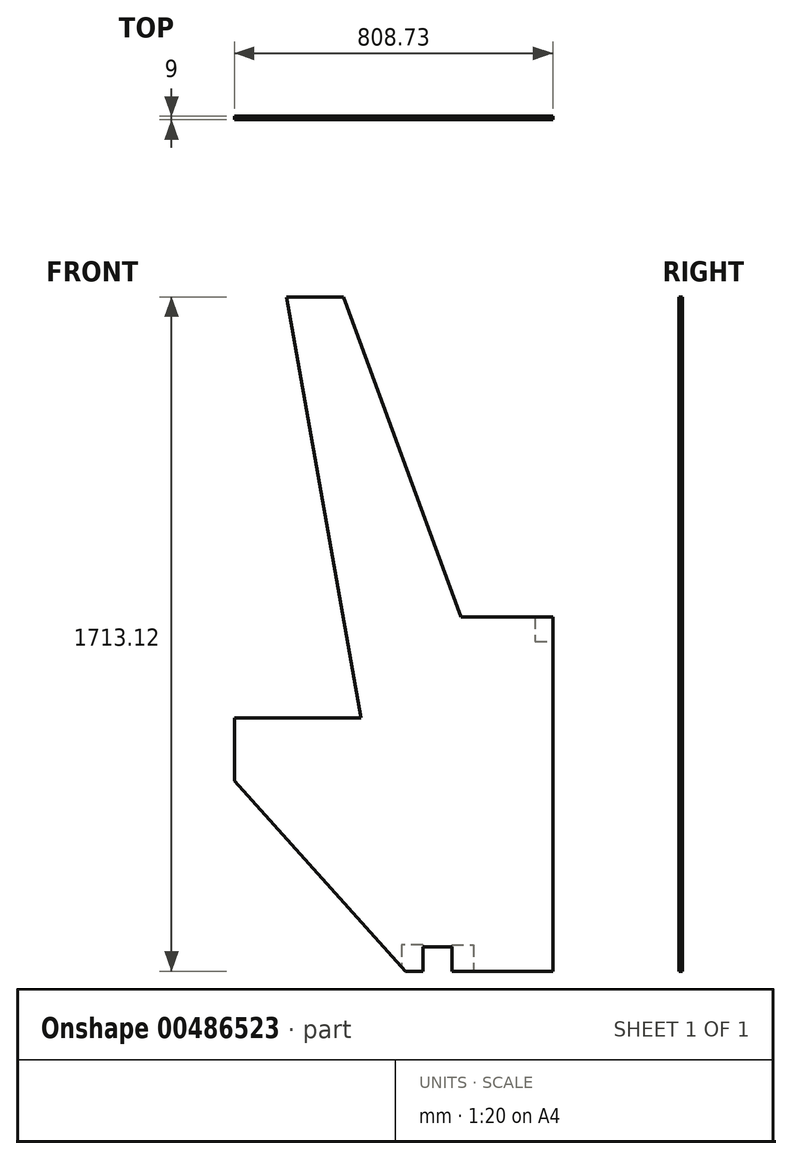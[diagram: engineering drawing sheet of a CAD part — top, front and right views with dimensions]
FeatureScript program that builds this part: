
annotation { "Feature Type Name" : "Feature", "Feature Type Description" : "" }
export const myFeature = defineFeature(function(context is Context, id is Id, definition is map)
    precondition{}
    {
        {
            var Q0;
            Q0=qCreatedBy(makeId("Front.planeOp"),FACE);
            var sketch = newSketch(context, id + "F0", { "sketchPlane" : qUnion([Q0])});
            skLineSegment(sketch, "E0", {"start": v(0, 0) * mm, "end": v(-435.1, 482.9) * mm});
            skLineSegment(sketch, "E1", {"start": v(-435.1, 482.9) * mm, "end": v(-435.1, 642.9) * mm});
            skLineSegment(sketch, "E2", {"start": v(-435.1, 642.9) * mm, "end": v(-113.1, 642.9) * mm});
            skLineSegment(sketch, "E3", {"start": v(-113.1, 642.9) * mm, "end": v(-303.35, 1713.12) * mm});
            skLineSegment(sketch, "E4", {"start": v(-303.35, 1713.12) * mm, "end": v(-157.35, 1713.12) * mm});
            skLineSegment(sketch, "E5", {"start": v(-157.35, 1713.12) * mm, "end": v(140.63, 900) * mm});
            skLineSegment(sketch, "E6", {"start": v(140.63, 900) * mm, "end": v(373.63, 900) * mm});
            skLineSegment(sketch, "E7", {"start": v(373.63, 900) * mm, "end": v(373.63, 0) * mm});
            skLineSegment(sketch, "E8", {"start": v(0, 0) * mm, "end": v(44, 0) * mm});
            skLineSegment(sketch, "E9", {"start": v(328.63, 900) * mm, "end": v(328.63, 838) * mm});
            skLineSegment(sketch, "E10", {"start": v(328.63, 838) * mm, "end": v(373.63, 838) * mm});
            skLineSegment(sketch, "E11", {"start": v(44, 0) * mm, "end": v(44, 62) * mm});
            skLineSegment(sketch, "E12", {"start": v(44, 62) * mm, "end": v(117, 62) * mm});
            skLineSegment(sketch, "E13", {"start": v(117, 62) * mm, "end": v(117, 0) * mm});
            skLineSegment(sketch, "E14.trimOffspring", {"start": v(117, 0) * mm, "end": v(373.63, 0) * mm});
            skLineSegment(sketch, "E15", {"start": v(44, 67) * mm, "end": v(44, 62) * mm});
            skLineSegment(sketch, "E16", {"start": v(44, 67) * mm, "end": v(-11, 67) * mm});
            skLineSegment(sketch, "E17", {"start": v(-11, 67) * mm, "end": v(-11, 12.2) * mm});
            skLineSegment(sketch, "E18", {"start": v(117, 67) * mm, "end": v(117, 62) * mm});
            skLineSegment(sketch, "E19", {"start": v(117, 67) * mm, "end": v(172, 67) * mm});
            skLineSegment(sketch, "E20", {"start": v(172, 67) * mm, "end": v(172, 0) * mm});
            skSolve(sketch);
        }
        {
            var Q0;
            {var subQ7=sQuery(id+"F0.wireOp",EDGE,"E1");Q0=makeQuery(id+"F0.imprint","IMPRINT",FACE,{"disambiguationData":[TD([[makeQuery(id+"F0.imprint","IMPRINT",EDGE,{"derivedFrom":subQ7}),-1.0]])]});}
            var Q1;
            {var subQ0=sQuery(id+"F0.wireOp",EDGE,"E8");Q1=makeQuery(id+"F0.imprint","IMPRINT",FACE,{"disambiguationData":[TD([[makeQuery(id+"F0.imprint","IMPRINT",EDGE,{"derivedFrom":subQ0}),1.0]])]});}
            var Q2;
            {var subQ1=sQuery(id+"F0.wireOp",EDGE,"E13");Q2=makeQuery(id+"F0.imprint","IMPRINT",FACE,{"disambiguationData":[TD([[makeQuery(id+"F0.imprint","IMPRINT",EDGE,{"derivedFrom":subQ1}),1.0]])]});}
            var Q3;
            {var subQ3=sQuery(id+"F0.wireOp",EDGE,"E9");Q3=makeQuery(id+"F0.imprint","IMPRINT",FACE,{"disambiguationData":[TD([[makeQuery(id+"F0.imprint","IMPRINT",EDGE,{"derivedFrom":subQ3}),1.0]])]});}
            extrude(context, id + "F1", {"entities" : qUnion([Q0, Q1, Q2, Q3]), "depth" : 9 * mm, "offsetDistance" : 25 * mm});
        }
        {
            var Q0;
            {var subQ3=sQuery(id+"F0.wireOp",EDGE,"E9");Q0=makeQuery(id+"F0.imprint","IMPRINT",FACE,{"disambiguationData":[TD([[makeQuery(id+"F0.imprint","IMPRINT",EDGE,{"derivedFrom":subQ3}),1.0]])]});}
            var Q1;
            {var subQ0=sQuery(id+"F0.wireOp",EDGE,"E8");Q1=makeQuery(id+"F0.imprint","IMPRINT",FACE,{"disambiguationData":[TD([[makeQuery(id+"F0.imprint","IMPRINT",EDGE,{"derivedFrom":subQ0}),1.0]])]});}
            var Q2;
            {var subQ1=sQuery(id+"F0.wireOp",EDGE,"E13");Q2=makeQuery(id+"F0.imprint","IMPRINT",FACE,{"disambiguationData":[TD([[makeQuery(id+"F0.imprint","IMPRINT",EDGE,{"derivedFrom":subQ1}),1.0]])]});}
            extrude(context, id + "F2", {"entities" : qUnion([Q0, Q1, Q2]), "operationType" : NewBodyOperationType.REMOVE, "depth" : 5 * mm, "offsetDistance" : 25 * mm});
        }
    });
